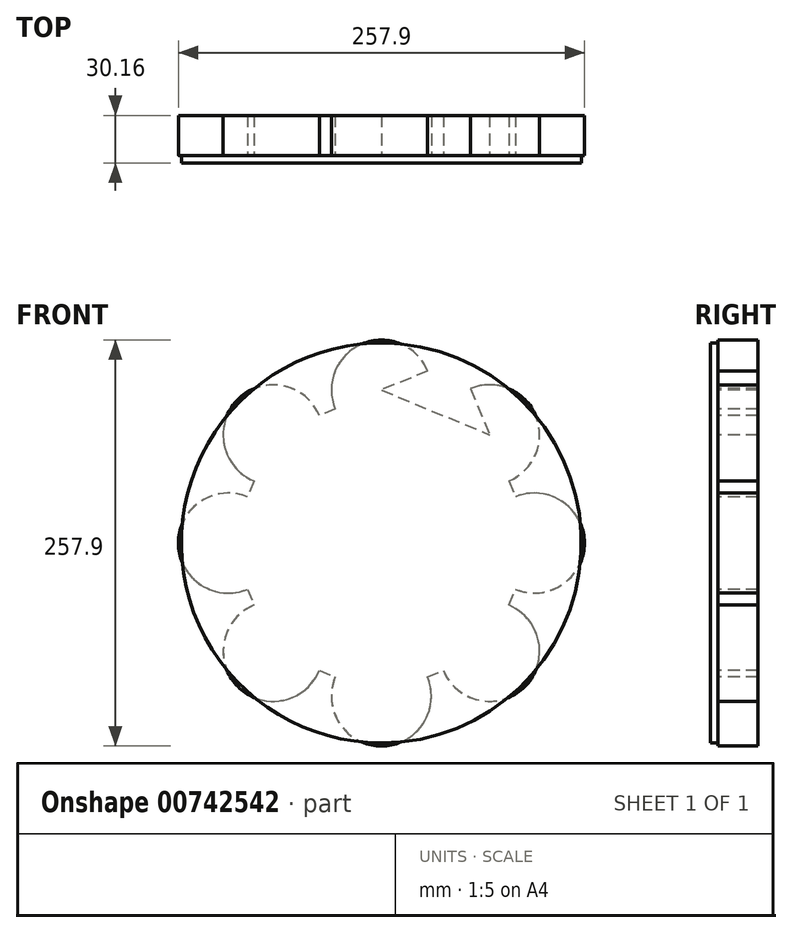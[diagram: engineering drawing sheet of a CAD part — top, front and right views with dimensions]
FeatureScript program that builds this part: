
annotation { "Feature Type Name" : "Feature", "Feature Type Description" : "" }
export const myFeature = defineFeature(function(context is Context, id is Id, definition is map)
    precondition{}
    {
        {
            var Q0;
            Q0=qCreatedBy(makeId("Front.planeOp"),FACE);
            var sketch = newSketch(context, id + "F0", { "sketchPlane" : qUnion([Q0])});
            skCircle(sketch, "E0", {"center": v(0, 0) * mm, "radius": 127 * mm});
            skSolve(sketch);
        }
        {
            var Q0;
            Q0=makeQuery(id+"F0.imprint","IMPRINT",FACE,{"disambiguationData":[TD([[makeQuery(id+"F0.imprint","IMPRINT",EDGE,{"derivedFrom":sQuery(id+"F0.wireOp",EDGE,"E0")}),1.0]])]});
            extrude(context, id + "F1", {"entities" : qUnion([Q0]), "depth" : 4.76 * mm, "offsetDistance" : 25.4 * mm});
        }
        {
            var Q0;
            Q0=qCreatedBy(makeId("Front.planeOp"),FACE);
            var sketch = newSketch(context, id + "F2", { "sketchPlane" : qUnion([Q0])});
            skCircle(sketch, "E1.cCircle", {"center": v(0, 0) * mm, "radius": 117.33 * mm, "construction": true});
            skLineSegment(sketch, "E1.0", {"start": v(-117.33, 48.6) * mm, "end": v(-48.6, 117.33) * mm});
            skLineSegment(sketch, "E1.1", {"start": v(-48.6, 117.33) * mm, "end": v(48.6, 117.33) * mm});
            skLineSegment(sketch, "E1.2", {"start": v(48.6, 117.33) * mm, "end": v(117.33, 48.6) * mm});
            skLineSegment(sketch, "E1.3", {"start": v(117.33, 48.6) * mm, "end": v(117.33, -48.6) * mm});
            skLineSegment(sketch, "E1.4", {"start": v(117.33, -48.6) * mm, "end": v(48.6, -117.33) * mm});
            skLineSegment(sketch, "E1.5", {"start": v(48.6, -117.33) * mm, "end": v(-48.6, -117.33) * mm});
            skLineSegment(sketch, "E1.6", {"start": v(-48.6, -117.33) * mm, "end": v(-117.33, -48.6) * mm});
            skLineSegment(sketch, "E1.7", {"start": v(-117.33, -48.6) * mm, "end": v(-117.33, 48.6) * mm});
            skPoint(sketch, "E1.0.midPoint", {"position": v(-82.97, 82.97) * mm});
            skLineSegment(sketch, "E2", {"start": v(48.6, 117.33) * mm, "end": v(-117.33, 48.6) * mm});
            skLineSegment(sketch, "E3", {"start": v(-48.6, 117.33) * mm, "end": v(-117.33, -48.6) * mm});
            skLineSegment(sketch, "E4", {"start": v(-117.33, 48.6) * mm, "end": v(-48.6, -117.33) * mm});
            skLineSegment(sketch, "E5", {"start": v(-117.33, -48.6) * mm, "end": v(48.6, -117.33) * mm});
            skLineSegment(sketch, "E6", {"start": v(-48.6, -117.33) * mm, "end": v(117.33, -48.6) * mm});
            skLineSegment(sketch, "E7", {"start": v(48.6, 117.33) * mm, "end": v(117.33, -48.6) * mm});
            skLineSegment(sketch, "E8", {"start": v(-48.6, 117.33) * mm, "end": v(117.33, 48.6) * mm});
            skLineSegment(sketch, "E9", {"start": v(48.6, -117.33) * mm, "end": v(117.33, 48.6) * mm});
            skCircle(sketch, "E10", {"center": v(0, 97.2) * mm, "radius": 31.75 * mm});
            skCircle(sketch, "E11", {"center": v(-68.73, 68.73) * mm, "radius": 31.75 * mm});
            skCircle(sketch, "E12", {"center": v(-97.2, 0) * mm, "radius": 31.75 * mm});
            skCircle(sketch, "E13", {"center": v(-68.73, -68.73) * mm, "radius": 31.75 * mm});
            skCircle(sketch, "E14", {"center": v(0, -97.2) * mm, "radius": 31.75 * mm});
            skCircle(sketch, "E15", {"center": v(68.73, -68.73) * mm, "radius": 31.75 * mm});
            skCircle(sketch, "E16", {"center": v(68.73, 68.73) * mm, "radius": 31.75 * mm});
            skCircle(sketch, "E17", {"center": v(97.2, 0) * mm, "radius": 31.75 * mm});
            skSolve(sketch);
        }
        {
            var Q0;
            {var subQ0=sQuery(id+"F2.wireOp",EDGE,"E13");var subQ1=sQuery(id+"F2.wireOp",EDGE,"E4");var subQ2=makeQuery(id+"F2.imprint","INTERSECT",VERTEX,{"disambiguationData":[OD(0.0)],"derivedFrom":[subQ1,subQ0]});Q0=makeQuery(id+"F2.imprint","IMPRINT",FACE,{"disambiguationData":[TD([[makeQuery(id+"F2.imprint","IMPRINT",EDGE,{"disambiguationData":[TD([[subQ2,-1.0]])],"derivedFrom":subQ1}),1.0]])]});}
            var Q1;
            {var subQ0=sQuery(id+"F2.wireOp",EDGE,"E5");var subQ1=sQuery(id+"F2.wireOp",EDGE,"E4");var subQ2=makeQuery(id+"F2.imprint","INTERSECT",VERTEX,{"derivedFrom":[subQ1,subQ0]});Q1=makeQuery(id+"F2.imprint","IMPRINT",FACE,{"disambiguationData":[TD([[makeQuery(id+"F2.imprint","IMPRINT",EDGE,{"disambiguationData":[TD([[subQ2,-1.0]])],"derivedFrom":subQ1}),1.0]])]});}
            var Q2;
            {var subQ0=sQuery(id+"F2.wireOp",EDGE,"E13");var subQ1=sQuery(id+"F2.wireOp",EDGE,"E4");var subQ2=makeQuery(id+"F2.imprint","INTERSECT",VERTEX,{"disambiguationData":[OD(0.0)],"derivedFrom":[subQ1,subQ0]});Q2=makeQuery(id+"F2.imprint","IMPRINT",FACE,{"disambiguationData":[TD([[makeQuery(id+"F2.imprint","IMPRINT",EDGE,{"disambiguationData":[TD([[subQ2,-1.0]])],"derivedFrom":subQ1}),-1.0]])]});}
            var Q3;
            {var subQ3=sQuery(id+"F2.wireOp",EDGE,"E13");var subQ5=sQuery(id+"F2.wireOp",EDGE,"E1.6");var subQ6=makeQuery(id+"F2.imprint","INTERSECT",VERTEX,{"disambiguationData":[OD(0.0)],"derivedFrom":[subQ5,subQ3]});Q3=makeQuery(id+"F2.imprint","IMPRINT",FACE,{"disambiguationData":[TD([[makeQuery(id+"F2.imprint","IMPRINT",EDGE,{"disambiguationData":[TD([[subQ6,-1.0]])],"derivedFrom":subQ5}),-1.0]])]});}
            var Q4;
            {var subQ0=sQuery(id+"F2.wireOp",EDGE,"E13");var subQ1=sQuery(id+"F2.wireOp",EDGE,"E1.6");var subQ2=makeQuery(id+"F2.imprint","INTERSECT",VERTEX,{"disambiguationData":[OD(0.0)],"derivedFrom":[subQ1,subQ0]});Q4=makeQuery(id+"F2.imprint","IMPRINT",FACE,{"disambiguationData":[TD([[makeQuery(id+"F2.imprint","IMPRINT",EDGE,{"disambiguationData":[TD([[subQ2,-1.0]])],"derivedFrom":subQ1}),1.0]])]});}
            var Q5;
            {var subQ0=sQuery(id+"F2.wireOp",EDGE,"E4");var subQ1=sQuery(id+"F2.wireOp",EDGE,"E3");var subQ2=makeQuery(id+"F2.imprint","INTERSECT",VERTEX,{"derivedFrom":[subQ1,subQ0]});Q5=makeQuery(id+"F2.imprint","IMPRINT",FACE,{"disambiguationData":[TD([[makeQuery(id+"F2.imprint","IMPRINT",EDGE,{"disambiguationData":[TD([[subQ2,-1.0]])],"derivedFrom":subQ1}),1.0]])]});}
            var Q6;
            {var subQ0=sQuery(id+"F2.wireOp",EDGE,"E12");var subQ1=sQuery(id+"F2.wireOp",EDGE,"E3");var subQ2=makeQuery(id+"F2.imprint","INTERSECT",VERTEX,{"disambiguationData":[OD(0.0)],"derivedFrom":[subQ1,subQ0]});Q6=makeQuery(id+"F2.imprint","IMPRINT",FACE,{"disambiguationData":[TD([[makeQuery(id+"F2.imprint","IMPRINT",EDGE,{"disambiguationData":[TD([[subQ2,-1.0]])],"derivedFrom":subQ1}),1.0]])]});}
            var Q7;
            {var subQ0=sQuery(id+"F2.wireOp",EDGE,"E12");var subQ1=sQuery(id+"F2.wireOp",EDGE,"E3");var subQ2=makeQuery(id+"F2.imprint","INTERSECT",VERTEX,{"disambiguationData":[OD(0.0)],"derivedFrom":[subQ1,subQ0]});Q7=makeQuery(id+"F2.imprint","IMPRINT",FACE,{"disambiguationData":[TD([[makeQuery(id+"F2.imprint","IMPRINT",EDGE,{"disambiguationData":[TD([[subQ2,-1.0]])],"derivedFrom":subQ1}),-1.0]])]});}
            var Q8;
            {var subQ0=sQuery(id+"F2.wireOp",EDGE,"E12");var subQ1=sQuery(id+"F2.wireOp",EDGE,"E1.7");var subQ8=makeQuery(id+"F2.imprint","INTERSECT",VERTEX,{"disambiguationData":[OD(0.0)],"derivedFrom":[subQ1,subQ0]});Q8=makeQuery(id+"F2.imprint","IMPRINT",FACE,{"disambiguationData":[TD([[makeQuery(id+"F2.imprint","IMPRINT",EDGE,{"disambiguationData":[TD([[subQ8,-1.0]])],"derivedFrom":subQ1}),-1.0]])]});}
            var Q9;
            {var subQ0=sQuery(id+"F2.wireOp",EDGE,"E12");var subQ1=sQuery(id+"F2.wireOp",EDGE,"E1.7");var subQ2=makeQuery(id+"F2.imprint","INTERSECT",VERTEX,{"disambiguationData":[OD(0.0)],"derivedFrom":[subQ1,subQ0]});Q9=makeQuery(id+"F2.imprint","IMPRINT",FACE,{"disambiguationData":[TD([[makeQuery(id+"F2.imprint","IMPRINT",EDGE,{"disambiguationData":[TD([[subQ2,-1.0]])],"derivedFrom":subQ1}),1.0]])]});}
            var Q10;
            {var subQ0=sQuery(id+"F2.wireOp",EDGE,"E3");var subQ1=sQuery(id+"F2.wireOp",EDGE,"E2");var subQ2=makeQuery(id+"F2.imprint","INTERSECT",VERTEX,{"derivedFrom":[subQ1,subQ0]});Q10=makeQuery(id+"F2.imprint","IMPRINT",FACE,{"disambiguationData":[TD([[makeQuery(id+"F2.imprint","IMPRINT",EDGE,{"disambiguationData":[TD([[subQ2,-1.0]])],"derivedFrom":subQ1}),1.0]])]});}
            var Q11;
            {var subQ0=sQuery(id+"F2.wireOp",EDGE,"E11");var subQ1=sQuery(id+"F2.wireOp",EDGE,"E2");var subQ2=makeQuery(id+"F2.imprint","INTERSECT",VERTEX,{"disambiguationData":[OD(0.0)],"derivedFrom":[subQ1,subQ0]});Q11=makeQuery(id+"F2.imprint","IMPRINT",FACE,{"disambiguationData":[TD([[makeQuery(id+"F2.imprint","IMPRINT",EDGE,{"disambiguationData":[TD([[subQ2,-1.0]])],"derivedFrom":subQ1}),1.0]])]});}
            var Q12;
            {var subQ0=sQuery(id+"F2.wireOp",EDGE,"E11");var subQ1=sQuery(id+"F2.wireOp",EDGE,"E2");var subQ2=makeQuery(id+"F2.imprint","INTERSECT",VERTEX,{"disambiguationData":[OD(0.0)],"derivedFrom":[subQ1,subQ0]});Q12=makeQuery(id+"F2.imprint","IMPRINT",FACE,{"disambiguationData":[TD([[makeQuery(id+"F2.imprint","IMPRINT",EDGE,{"disambiguationData":[TD([[subQ2,-1.0]])],"derivedFrom":subQ1}),-1.0]])]});}
            var Q13;
            {var subQ0=sQuery(id+"F2.wireOp",EDGE,"E11");var subQ1=sQuery(id+"F2.wireOp",EDGE,"E1.0");var subQ8=makeQuery(id+"F2.imprint","INTERSECT",VERTEX,{"disambiguationData":[OD(0.0)],"derivedFrom":[subQ1,subQ0]});Q13=makeQuery(id+"F2.imprint","IMPRINT",FACE,{"disambiguationData":[TD([[makeQuery(id+"F2.imprint","IMPRINT",EDGE,{"disambiguationData":[TD([[subQ8,-1.0]])],"derivedFrom":subQ1}),-1.0]])]});}
            var Q14;
            {var subQ0=sQuery(id+"F2.wireOp",EDGE,"E11");var subQ1=sQuery(id+"F2.wireOp",EDGE,"E1.0");var subQ2=makeQuery(id+"F2.imprint","INTERSECT",VERTEX,{"disambiguationData":[OD(0.0)],"derivedFrom":[subQ1,subQ0]});Q14=makeQuery(id+"F2.imprint","IMPRINT",FACE,{"disambiguationData":[TD([[makeQuery(id+"F2.imprint","IMPRINT",EDGE,{"disambiguationData":[TD([[subQ2,-1.0]])],"derivedFrom":subQ1}),1.0]])]});}
            var Q15;
            {var subQ0=sQuery(id+"F2.wireOp",EDGE,"E8");var subQ1=sQuery(id+"F2.wireOp",EDGE,"E2");var subQ2=makeQuery(id+"F2.imprint","INTERSECT",VERTEX,{"derivedFrom":[subQ1,subQ0]});Q15=makeQuery(id+"F2.imprint","IMPRINT",FACE,{"disambiguationData":[TD([[makeQuery(id+"F2.imprint","IMPRINT",EDGE,{"disambiguationData":[TD([[subQ2,-1.0]])],"derivedFrom":subQ1}),1.0]])]});}
            var Q16;
            {var subQ0=sQuery(id+"F2.wireOp",EDGE,"E8");var subQ1=sQuery(id+"F2.wireOp",EDGE,"E2");var subQ2=makeQuery(id+"F2.imprint","INTERSECT",VERTEX,{"derivedFrom":[subQ1,subQ0]});Q16=makeQuery(id+"F2.imprint","IMPRINT",FACE,{"disambiguationData":[TD([[makeQuery(id+"F2.imprint","IMPRINT",EDGE,{"disambiguationData":[TD([[subQ2,-1.0]])],"derivedFrom":subQ1}),-1.0]])]});}
            var Q17;
            {var subQ0=sQuery(id+"F2.wireOp",EDGE,"E10");var subQ1=sQuery(id+"F2.wireOp",EDGE,"E2");var subQ2=makeQuery(id+"F2.imprint","INTERSECT",VERTEX,{"disambiguationData":[OD(0.0)],"derivedFrom":[subQ1,subQ0]});Q17=makeQuery(id+"F2.imprint","IMPRINT",FACE,{"disambiguationData":[TD([[makeQuery(id+"F2.imprint","IMPRINT",EDGE,{"disambiguationData":[TD([[subQ2,-1.0]])],"derivedFrom":subQ1}),1.0]])]});}
            var Q18;
            {var subQ3=sQuery(id+"F2.wireOp",EDGE,"E10");var subQ5=sQuery(id+"F2.wireOp",EDGE,"E1.1");var subQ8=makeQuery(id+"F2.imprint","INTERSECT",VERTEX,{"disambiguationData":[OD(0.0)],"derivedFrom":[subQ5,subQ3]});Q18=makeQuery(id+"F2.imprint","IMPRINT",FACE,{"disambiguationData":[TD([[makeQuery(id+"F2.imprint","IMPRINT",EDGE,{"disambiguationData":[TD([[subQ8,-1.0]])],"derivedFrom":subQ5}),-1.0]])]});}
            var Q19;
            {var subQ0=sQuery(id+"F2.wireOp",EDGE,"E10");var subQ1=sQuery(id+"F2.wireOp",EDGE,"E1.1");var subQ2=makeQuery(id+"F2.imprint","INTERSECT",VERTEX,{"disambiguationData":[OD(0.0)],"derivedFrom":[subQ1,subQ0]});Q19=makeQuery(id+"F2.imprint","IMPRINT",FACE,{"disambiguationData":[TD([[makeQuery(id+"F2.imprint","IMPRINT",EDGE,{"disambiguationData":[TD([[subQ2,-1.0]])],"derivedFrom":subQ1}),1.0]])]});}
            var Q20;
            {var subQ0=sQuery(id+"F2.wireOp",EDGE,"E8");var subQ1=sQuery(id+"F2.wireOp",EDGE,"E7");var subQ2=makeQuery(id+"F2.imprint","INTERSECT",VERTEX,{"derivedFrom":[subQ1,subQ0]});Q20=makeQuery(id+"F2.imprint","IMPRINT",FACE,{"disambiguationData":[TD([[makeQuery(id+"F2.imprint","IMPRINT",EDGE,{"disambiguationData":[TD([[subQ2,-1.0]])],"derivedFrom":subQ1}),-1.0]])]});}
            var Q21;
            {var subQ0=sQuery(id+"F2.wireOp",EDGE,"E16");var subQ1=sQuery(id+"F2.wireOp",EDGE,"E7");var subQ2=makeQuery(id+"F2.imprint","INTERSECT",VERTEX,{"disambiguationData":[OD(0.0)],"derivedFrom":[subQ1,subQ0]});Q21=makeQuery(id+"F2.imprint","IMPRINT",FACE,{"disambiguationData":[TD([[makeQuery(id+"F2.imprint","IMPRINT",EDGE,{"disambiguationData":[TD([[subQ2,-1.0]])],"derivedFrom":subQ1}),-1.0]])]});}
            var Q22;
            {var subQ0=sQuery(id+"F2.wireOp",EDGE,"E16");var subQ1=sQuery(id+"F2.wireOp",EDGE,"E1.2");var subQ2=makeQuery(id+"F2.imprint","INTERSECT",VERTEX,{"disambiguationData":[OD(0.0)],"derivedFrom":[subQ1,subQ0]});Q22=makeQuery(id+"F2.imprint","IMPRINT",FACE,{"disambiguationData":[TD([[makeQuery(id+"F2.imprint","IMPRINT",EDGE,{"disambiguationData":[TD([[subQ2,-1.0]])],"derivedFrom":subQ1}),-1.0]])]});}
            var Q23;
            {var subQ0=sQuery(id+"F2.wireOp",EDGE,"E8");var subQ1=sQuery(id+"F2.wireOp",EDGE,"E7");var subQ2=makeQuery(id+"F2.imprint","INTERSECT",VERTEX,{"derivedFrom":[subQ1,subQ0]});Q23=makeQuery(id+"F2.imprint","IMPRINT",FACE,{"disambiguationData":[TD([[makeQuery(id+"F2.imprint","IMPRINT",EDGE,{"disambiguationData":[TD([[subQ2,-1.0]])],"derivedFrom":subQ1}),1.0]])]});}
            var Q24;
            {var subQ0=sQuery(id+"F2.wireOp",EDGE,"E16");var subQ1=sQuery(id+"F2.wireOp",EDGE,"E1.2");var subQ2=makeQuery(id+"F2.imprint","INTERSECT",VERTEX,{"disambiguationData":[OD(0.0)],"derivedFrom":[subQ1,subQ0]});Q24=makeQuery(id+"F2.imprint","IMPRINT",FACE,{"disambiguationData":[TD([[makeQuery(id+"F2.imprint","IMPRINT",EDGE,{"disambiguationData":[TD([[subQ2,-1.0]])],"derivedFrom":subQ1}),1.0]])]});}
            var Q25;
            {var subQ0=sQuery(id+"F2.wireOp",EDGE,"E17");var subQ1=sQuery(id+"F2.wireOp",EDGE,"E7");var subQ2=makeQuery(id+"F2.imprint","INTERSECT",VERTEX,{"disambiguationData":[OD(0.0)],"derivedFrom":[subQ1,subQ0]});Q25=makeQuery(id+"F2.imprint","IMPRINT",FACE,{"disambiguationData":[TD([[makeQuery(id+"F2.imprint","IMPRINT",EDGE,{"disambiguationData":[TD([[subQ2,-1.0]])],"derivedFrom":subQ1}),-1.0]])]});}
            var Q26;
            {var subQ0=sQuery(id+"F2.wireOp",EDGE,"E17");var subQ1=sQuery(id+"F2.wireOp",EDGE,"E1.3");var subQ2=makeQuery(id+"F2.imprint","INTERSECT",VERTEX,{"disambiguationData":[OD(0.0)],"derivedFrom":[subQ1,subQ0]});Q26=makeQuery(id+"F2.imprint","IMPRINT",FACE,{"disambiguationData":[TD([[makeQuery(id+"F2.imprint","IMPRINT",EDGE,{"disambiguationData":[TD([[subQ2,-1.0]])],"derivedFrom":subQ1}),-1.0]])]});}
            var Q27;
            {var subQ0=sQuery(id+"F2.wireOp",EDGE,"E17");var subQ1=sQuery(id+"F2.wireOp",EDGE,"E7");var subQ2=makeQuery(id+"F2.imprint","INTERSECT",VERTEX,{"disambiguationData":[OD(0.0)],"derivedFrom":[subQ1,subQ0]});Q27=makeQuery(id+"F2.imprint","IMPRINT",FACE,{"disambiguationData":[TD([[makeQuery(id+"F2.imprint","IMPRINT",EDGE,{"disambiguationData":[TD([[subQ2,-1.0]])],"derivedFrom":subQ1}),1.0]])]});}
            var Q28;
            {var subQ0=sQuery(id+"F2.wireOp",EDGE,"E9");var subQ1=sQuery(id+"F2.wireOp",EDGE,"E7");var subQ2=makeQuery(id+"F2.imprint","INTERSECT",VERTEX,{"derivedFrom":[subQ1,subQ0]});Q28=makeQuery(id+"F2.imprint","IMPRINT",FACE,{"disambiguationData":[TD([[makeQuery(id+"F2.imprint","IMPRINT",EDGE,{"disambiguationData":[TD([[subQ2,-1.0]])],"derivedFrom":subQ1}),-1.0]])]});}
            var Q29;
            {var subQ0=sQuery(id+"F2.wireOp",EDGE,"E17");var subQ1=sQuery(id+"F2.wireOp",EDGE,"E1.3");var subQ2=makeQuery(id+"F2.imprint","INTERSECT",VERTEX,{"disambiguationData":[OD(0.0)],"derivedFrom":[subQ1,subQ0]});Q29=makeQuery(id+"F2.imprint","IMPRINT",FACE,{"disambiguationData":[TD([[makeQuery(id+"F2.imprint","IMPRINT",EDGE,{"disambiguationData":[TD([[subQ2,-1.0]])],"derivedFrom":subQ1}),1.0]])]});}
            var Q30;
            {var subQ0=sQuery(id+"F2.wireOp",EDGE,"E9");var subQ1=sQuery(id+"F2.wireOp",EDGE,"E6");var subQ2=makeQuery(id+"F2.imprint","INTERSECT",VERTEX,{"derivedFrom":[subQ1,subQ0]});Q30=makeQuery(id+"F2.imprint","IMPRINT",FACE,{"disambiguationData":[TD([[makeQuery(id+"F2.imprint","IMPRINT",EDGE,{"disambiguationData":[TD([[subQ2,-1.0]])],"derivedFrom":subQ1}),1.0]])]});}
            var Q31;
            {var subQ0=sQuery(id+"F2.wireOp",EDGE,"E15");var subQ1=sQuery(id+"F2.wireOp",EDGE,"E6");var subQ2=makeQuery(id+"F2.imprint","INTERSECT",VERTEX,{"disambiguationData":[OD(0.0)],"derivedFrom":[subQ1,subQ0]});Q31=makeQuery(id+"F2.imprint","IMPRINT",FACE,{"disambiguationData":[TD([[makeQuery(id+"F2.imprint","IMPRINT",EDGE,{"disambiguationData":[TD([[subQ2,-1.0]])],"derivedFrom":subQ1}),1.0]])]});}
            var Q32;
            {var subQ0=sQuery(id+"F2.wireOp",EDGE,"E15");var subQ1=sQuery(id+"F2.wireOp",EDGE,"E6");var subQ2=makeQuery(id+"F2.imprint","INTERSECT",VERTEX,{"disambiguationData":[OD(0.0)],"derivedFrom":[subQ1,subQ0]});Q32=makeQuery(id+"F2.imprint","IMPRINT",FACE,{"disambiguationData":[TD([[makeQuery(id+"F2.imprint","IMPRINT",EDGE,{"disambiguationData":[TD([[subQ2,-1.0]])],"derivedFrom":subQ1}),-1.0]])]});}
            var Q33;
            {var subQ0=sQuery(id+"F2.wireOp",EDGE,"E15");var subQ1=sQuery(id+"F2.wireOp",EDGE,"E1.4");var subQ2=makeQuery(id+"F2.imprint","INTERSECT",VERTEX,{"disambiguationData":[OD(0.0)],"derivedFrom":[subQ1,subQ0]});Q33=makeQuery(id+"F2.imprint","IMPRINT",FACE,{"disambiguationData":[TD([[makeQuery(id+"F2.imprint","IMPRINT",EDGE,{"disambiguationData":[TD([[subQ2,-1.0]])],"derivedFrom":subQ1}),-1.0]])]});}
            var Q34;
            {var subQ0=sQuery(id+"F2.wireOp",EDGE,"E15");var subQ1=sQuery(id+"F2.wireOp",EDGE,"E1.4");var subQ2=makeQuery(id+"F2.imprint","INTERSECT",VERTEX,{"disambiguationData":[OD(0.0)],"derivedFrom":[subQ1,subQ0]});Q34=makeQuery(id+"F2.imprint","IMPRINT",FACE,{"disambiguationData":[TD([[makeQuery(id+"F2.imprint","IMPRINT",EDGE,{"disambiguationData":[TD([[subQ2,-1.0]])],"derivedFrom":subQ1}),1.0]])]});}
            var Q35;
            {var subQ0=sQuery(id+"F2.wireOp",EDGE,"E14");var subQ1=sQuery(id+"F2.wireOp",EDGE,"E5");var subQ2=makeQuery(id+"F2.imprint","INTERSECT",VERTEX,{"disambiguationData":[OD(0.0)],"derivedFrom":[subQ1,subQ0]});Q35=makeQuery(id+"F2.imprint","IMPRINT",FACE,{"disambiguationData":[TD([[makeQuery(id+"F2.imprint","IMPRINT",EDGE,{"disambiguationData":[TD([[subQ2,-1.0]])],"derivedFrom":subQ1}),1.0]])]});}
            var Q36;
            {var subQ0=sQuery(id+"F2.wireOp",EDGE,"E6");var subQ1=sQuery(id+"F2.wireOp",EDGE,"E5");var subQ2=makeQuery(id+"F2.imprint","INTERSECT",VERTEX,{"derivedFrom":[subQ1,subQ0]});Q36=makeQuery(id+"F2.imprint","IMPRINT",FACE,{"disambiguationData":[TD([[makeQuery(id+"F2.imprint","IMPRINT",EDGE,{"disambiguationData":[TD([[subQ2,-1.0]])],"derivedFrom":subQ1}),1.0]])]});}
            var Q37;
            {var subQ0=sQuery(id+"F2.wireOp",EDGE,"E14");var subQ1=sQuery(id+"F2.wireOp",EDGE,"E5");var subQ2=makeQuery(id+"F2.imprint","INTERSECT",VERTEX,{"disambiguationData":[OD(0.0)],"derivedFrom":[subQ1,subQ0]});Q37=makeQuery(id+"F2.imprint","IMPRINT",FACE,{"disambiguationData":[TD([[makeQuery(id+"F2.imprint","IMPRINT",EDGE,{"disambiguationData":[TD([[subQ2,-1.0]])],"derivedFrom":subQ1}),-1.0]])]});}
            var Q38;
            {var subQ3=sQuery(id+"F2.wireOp",EDGE,"E14");var subQ5=sQuery(id+"F2.wireOp",EDGE,"E1.5");var subQ6=makeQuery(id+"F2.imprint","INTERSECT",VERTEX,{"disambiguationData":[OD(0.0)],"derivedFrom":[subQ5,subQ3]});Q38=makeQuery(id+"F2.imprint","IMPRINT",FACE,{"disambiguationData":[TD([[makeQuery(id+"F2.imprint","IMPRINT",EDGE,{"disambiguationData":[TD([[subQ6,-1.0]])],"derivedFrom":subQ5}),-1.0]])]});}
            var Q39;
            {var subQ0=sQuery(id+"F2.wireOp",EDGE,"E14");var subQ1=sQuery(id+"F2.wireOp",EDGE,"E1.5");var subQ2=makeQuery(id+"F2.imprint","INTERSECT",VERTEX,{"disambiguationData":[OD(0.0)],"derivedFrom":[subQ1,subQ0]});Q39=makeQuery(id+"F2.imprint","IMPRINT",FACE,{"disambiguationData":[TD([[makeQuery(id+"F2.imprint","IMPRINT",EDGE,{"disambiguationData":[TD([[subQ2,-1.0]])],"derivedFrom":subQ1}),1.0]])]});}
            extrude(context, id + "F3", {"entities" : qUnion([Q0, Q1, Q2, Q3, Q4, Q5, Q6, Q7, Q8, Q9, Q10, Q11, Q12, Q13, Q14, Q15, Q16, Q17, Q18, Q19, Q20, Q21, Q22, Q23, Q24, Q25, Q26, Q27, Q28, Q29, Q30, Q31, Q32, Q33, Q34, Q35, Q36, Q37, Q38, Q39]), "operationType" : NewBodyOperationType.ADD, "oppositeDirection" : true, "depth" : 25.4 * mm, "offsetDistance" : 25.4 * mm});
        }
    });
